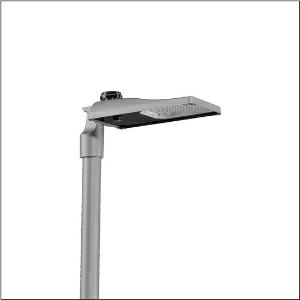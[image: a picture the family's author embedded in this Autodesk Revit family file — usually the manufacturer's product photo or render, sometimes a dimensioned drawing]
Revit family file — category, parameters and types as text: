
# Revit family: streetlight_sl_31_mini___p1_0a_5xh2a35m08ha_3b1d
name_source: partatom
category: Lighting Fixtures
units: mm (PartAtom-declared; Revit-internal decimal feet)

## family parameters
Cut with Voids When Loaded = No
Host = Face
Light Source = No
Part Type = Normal
Room Calculation Point = No
Round Connector Dimension = Use Diameter
Shared = No

## types (1)
- --- (1 x LED, 8970 lm, 68.2 W, 3000K)
    Apparent Load = 68 VA
    CIE Flux Codes = 23 55 94 100 100
    Color Rendering = 70
    Color Temperature = 3000K
    Default Elevation = 1800 mm
    Description = Streetlight SL 31 mini, mast luminaire, primary light control with lens, of PMMA, primary optical cover: cover, of toughened safety glass, transparent, light distribution: P1.0a, light emission: direct distribution, primary light characteristic: asymmetric, installation type: post-top, side-entry, LED, High Power LED, rated luminous flux: 8.970lm, luminous efficacy: 132lm/W, light colour: 730, colour temperature: 3000K, control: presetting dimming linear, flexible luminous flux parameterisation, time-dependent luminous flux control, constant luminous flux control, intelligent temperature release in ECG and LED module, overheat protection, with cable H07RN-F 3x 1.5mm², mains connection: 220..240V, AC, 50/60Hz, connection cable pre-assembled, cable length: 8,5m, start of lifetime: 68W, end of service life: 74W, reduction: 30W, luminaire housing, of diecast aluminium, powder-coated, Siteco® metallic grey (DB 702S), corrosivity category C5 high according to DIN EN ISO 12944, no sealing on luminaire upper side, inclination: -15°..+20° (post-top) | -20°..+20° (side-entry), adjustable in 5° steps, mast flange (76/60mm) included as standard, multi-level sealing system, sealing non-destructively replaceable, Smart Interface below, protection rating (complete): IP66, insulation class (complete): insulation class I (protective earthing), certification: CE, ENEC, ENEC+, VDE, UKCA, impact resistance: IK09, permissible operating ambient temperature for outdoor applications: -40..+50°C, standard-compliant lighting for roads and squares, packaging unit: 1 piece

Light Distribution: P1.0a
    Height = 76 mm
    Lamp = 1 x LED
    Lamp Light Flux = 8970 lm
    Lamp Power = 68.2 W
    Lamp count = 1
    Length = 547 mm
    Luminous efficacy = 132 lm/W
    Manufacturer = Siteco
    ModVariant = No
    Model = 5XH2A35M08HA
    Number of Poles = 1
    OnlyDefault = Yes
    Power Factor = 1
    Product Name = Streetlight SL 31 mini | P1.0a
    Product group = mast luminaire | pylon top
    ProductGroupID = 6100
    Protection Class = Protection class I
    Protection Degree = IP 66
    RLX_Detail_Level = 1
    RLX_Emergency_Light_Flux = 0 lm
    RLX_Emergency_Type = 0
    RLX_Emergency_Type_DB = No
    RlxData = <blob elided: 40181 chars, md5=cacddea3>
    Socket = socket
    Standby Power = 0 W
    System Light Flux = 8970 lm
    System Power = 68 W
    Type Comments = factory setting: luminous flux: 100 % | dim-lin: 254 | 692 mA
    Type Image = l_1300324.jpg
    URL = http://relux.com
    VarID = @adj_017347
    Voltage = 0 V
    Weight = 0.00 kg
    Width = 265 mm

## geometry (parser evidence)
native form markers: Blend x4, Sweep x7
no freeform markers — native parametric forms only
